# Revit family: IEK_Кронштейн для мачты_150мм
name_source: partatom
category: Обобщенные модели
units: mm (PartAtom-declared; Revit-internal decimal feet)

## family parameters
Может служить основой для арматурных стержней = Нет
Общий = Да
Основа = Грань
При загрузке вырезать с полостями = Нет
Размер круглого соединителя = Использовать диаметр
Тип детали = Нормальный
Точка расчета площади = Нет

## types (2) — shared parameters
ADSK_URL страницы изделия = https://www.iek.ru
ADSK_Версия Revit = 2019
ADSK_Версия семейства = 1.0
ADSK_Группирование = VIII. ЭЛЕМЕНТЫ ВНЕШНЕЙ МОЛНИЕЗАЩИТЫ
ADSK_Единица измерения = шт
ADSK_Завод-изготовитель = IEK
ADSK_Материал = Окраска - RAL 7035, светло-серый
ADSK_Материал наименование = Сталь
IEK_URL = https://www.iek.ru
KSI_CMa_Строительные материалы = 24.10.35.000.08.3.05.06-0001
zero-valued in all types: Отметка по умолчанию

## per-type parameters (varying)
| type | ADSK_Код изделия | ADSK_Масса | ADSK_Наименование | IEK_Описание | IEK_Цена за единицу | Высота |
| Облегченный | ZML10D-MB-02-150 | 0.65 | Кронштейн для мачты 150мм облегченный IEK | Кронштейн для мачты 150 мм облегченный товарного знака IEK используется для закрепления мачты молниеприемной на фасаде здания или других вертикальных поверхностях. Для крепления изделия имеют фланец с отверстиями диаметром 12 мм. | 1883.2 | 195 мм |
| Стандарт | ZML10D-MB-01-150 | 0.92 | Кронштейн для мачты 150мм стандарт IEK | Кронштейн для мачты 150 мм стандарт товарного знака IEK используется для закрепления мачты молниеприемной на фасаде здания или других вертикальных поверхностях. Для крепления изделия имеют фланец с отверстиями диаметром 12 мм. | 2118.6 | 196 мм |

## geometry (parser evidence)
native form markers: Blend x1
no freeform markers — native parametric forms only
